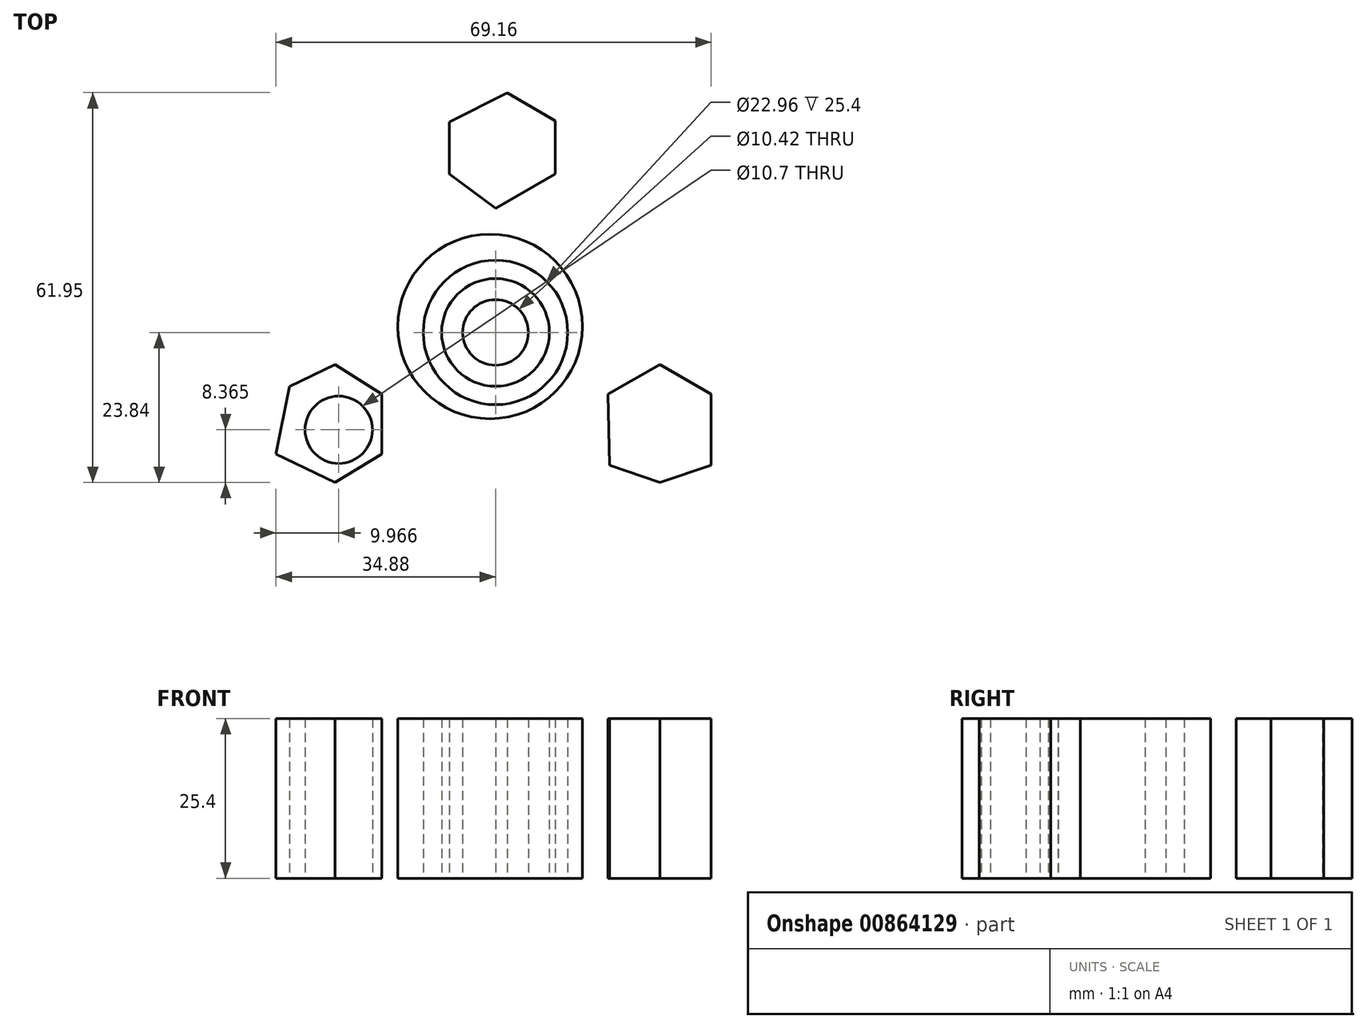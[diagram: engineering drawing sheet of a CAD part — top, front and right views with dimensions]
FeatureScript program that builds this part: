
annotation { "Feature Type Name" : "Feature", "Feature Type Description" : "" }
export const myFeature = defineFeature(function(context is Context, id is Id, definition is map)
    precondition{}
    {
        {
            var Q0;
            Q0=qCreatedBy(makeId("Top.planeOp"),FACE);
            var sketch = newSketch(context, id + "F0", { "sketchPlane" : qUnion([Q0])});
            skLineSegment(sketch, "E0", {"start": v(-11.04, 35.96) * mm, "end": v(-11.04, 44.95) * mm});
            skLineSegment(sketch, "E1", {"start": v(-11.04, 44.95) * mm, "end": v(-3.22, 42.4) * mm});
            skLineSegment(sketch, "E2", {"start": v(6.16, 42.4) * mm, "end": v(11.63, 44.95) * mm});
            skLineSegment(sketch, "E3", {"start": v(11.63, 44.95) * mm, "end": v(11.63, 37.52) * mm});
            skLineSegment(sketch, "E4", {"start": v(39.77, -8.2) * mm, "end": v(47.59, -14.27) * mm});
            skLineSegment(sketch, "E5", {"start": v(47.59, -14.27) * mm, "end": v(41.73, -18.37) * mm});
            skLineSegment(sketch, "E6", {"start": v(26.1, -31.66) * mm, "end": v(36.72, -37.23) * mm});
            skLineSegment(sketch, "E7", {"start": v(35.86, -27.75) * mm, "end": v(36.72, -37.23) * mm});
            skLineSegment(sketch, "E8", {"start": v(-37.62, -7.04) * mm, "end": v(-44.65, -12.7) * mm});
            skLineSegment(sketch, "E9", {"start": v(-44.65, -12.7) * mm, "end": v(-39.3, -15.5) * mm});
            skLineSegment(sketch, "E10", {"start": v(-34.88, -24.82) * mm, "end": v(-34.88, -32.05) * mm});
            skLineSegment(sketch, "E11", {"start": v(-34.88, -32.05) * mm, "end": v(-27.85, -29.12) * mm});
            skArc(sketch, "E12", {"start": v(-3.22, 42.4) * mm, "mid": v(1.47, 41.37) * mm, "end": v(6.16, 42.4) * mm});
            skArc(sketch, "E13", {"start": v(11.63, 16.8) * mm, "mid": v(15.34, 27.16) * mm, "end": v(11.63, 37.52) * mm});
            skArc(sketch, "E14", {"start": v(20.03, -2.35) * mm, "mid": v(19.22, 8.47) * mm, "end": v(11.63, 16.22) * mm});
            skArc(sketch, "E15", {"start": v(-11.04, 35.96) * mm, "mid": v(-13.25, 25.93) * mm, "end": v(-6.74, 17.98) * mm});
            skArc(sketch, "E16", {"start": v(-6.74, 17.98) * mm, "mid": v(-15.8, 11.02) * mm, "end": v(-18.86, 0) * mm});
            skArc(sketch, "E17", {"start": v(-18.86, 0) * mm, "mid": v(-29.8, 0.68) * mm, "end": v(-37.62, -7.04) * mm});
            skArc(sketch, "E18", {"start": v(-27.85, -29.12) * mm, "mid": v(-15.66, -27.36) * mm, "end": v(-10.84, -16.02) * mm});
            skArc(sketch, "E19", {"start": v(-10.84, -16.02) * mm, "mid": v(0.2, -21.41) * mm, "end": v(11.24, -16.02) * mm});
            skArc(sketch, "E20", {"start": v(11.24, -16.02) * mm, "mid": v(15.83, -26.53) * mm, "end": v(26.1, -31.66) * mm});
            skArc(sketch, "E21", {"start": v(39.38, -6.06) * mm, "mid": v(31.32, -1.24) * mm, "end": v(21.99, -2.35) * mm});
            skCircle(sketch, "E22", {"center": v(0, 0) * mm, "radius": 5.21 * mm});
            skCircle(sketch, "E23", {"center": v(0, 0) * mm, "radius": 8.56 * mm});
            skCircle(sketch, "E24", {"center": v(0, 0) * mm, "radius": 11.48 * mm});
            skCircle(sketch, "E25", {"center": v(-0.87, 0.95) * mm, "radius": 14.67 * mm});
            skLineSegment(sketch, "E26", {"start": v(-32.73, -8.6) * mm, "end": v(-25.5, -5.08) * mm});
            skLineSegment(sketch, "E27", {"start": v(-25.5, -5.08) * mm, "end": v(-18.07, -9.77) * mm});
            skLineSegment(sketch, "E28", {"start": v(-18.07, -9.77) * mm, "end": v(-18.07, -19.35) * mm});
            skLineSegment(sketch, "E29", {"start": v(-18.07, -19.35) * mm, "end": v(-25.5, -23.84) * mm});
            skLineSegment(sketch, "E30", {"start": v(-32.73, -8.6) * mm, "end": v(-34.88, -19.35) * mm});
            skLineSegment(sketch, "E31", {"start": v(-34.88, -19.35) * mm, "end": v(-25.5, -23.84) * mm});
            skLineSegment(sketch, "E32", {"start": v(17.88, -9.77) * mm, "end": v(26.1, -5.08) * mm});
            skLineSegment(sketch, "E33", {"start": v(26.1, -5.08) * mm, "end": v(34.28, -9.77) * mm});
            skLineSegment(sketch, "E34", {"start": v(34.28, -9.77) * mm, "end": v(34.28, -21.1) * mm});
            skLineSegment(sketch, "E35", {"start": v(34.28, -21.1) * mm, "end": v(26.1, -23.84) * mm});
            skLineSegment(sketch, "E36", {"start": v(26.1, -23.84) * mm, "end": v(18.14, -21.1) * mm});
            skLineSegment(sketch, "E37", {"start": v(18.14, -21.1) * mm, "end": v(17.88, -9.77) * mm});
            skCircle(sketch, "E38", {"center": v(25.31, -15.48) * mm, "radius": 6.67 * mm});
            skCircle(sketch, "E39", {"center": v(-24.91, -15.48) * mm, "radius": 5.35 * mm});
            skLineSegment(sketch, "E40", {"start": v(-7.33, 33.42) * mm, "end": v(-7.33, 25.2) * mm});
            skLineSegment(sketch, "E41", {"start": v(-7.33, 25.2) * mm, "end": v(0, 19.74) * mm});
            skLineSegment(sketch, "E42", {"start": v(0, 19.74) * mm, "end": v(9.48, 25.2) * mm});
            skLineSegment(sketch, "E43", {"start": v(9.48, 25.2) * mm, "end": v(9.48, 33.61) * mm});
            skLineSegment(sketch, "E44", {"start": v(9.48, 33.61) * mm, "end": v(1.86, 38.1) * mm});
            skLineSegment(sketch, "E45", {"start": v(1.86, 38.1) * mm, "end": v(-7.33, 33.42) * mm});
            skLineSegment(sketch, "E46", {"start": v(20.03, -2.35) * mm, "end": v(25.25, -1.24) * mm});
            skLineSegment(sketch, "E47", {"start": v(39.38, -6.06) * mm, "end": v(39.77, -8.2) * mm});
            skLineSegment(sketch, "E48", {"start": v(41.73, -18.37) * mm, "end": v(35.86, -27.75) * mm});
            skArc(sketch, "E49", {"start": v(-39.38, -17) * mm, "mid": v(-38.95, -21.96) * mm, "end": v(-34.88, -24.82) * mm});
            skSolve(sketch);
        }
        {
            var Q0;
            Q0=makeQuery(id+"F0.imprint","IMPRINT",FACE,{"disambiguationData":[TD([[makeQuery(id+"F0.imprint","IMPRINT",EDGE,{"derivedFrom":sQuery(id+"F0.wireOp",EDGE,"E24")}),-1.0]])]});
            var Q1;
            Q1=makeQuery(id+"F0.imprint","IMPRINT",FACE,{"disambiguationData":[TD([[makeQuery(id+"F0.imprint","IMPRINT",EDGE,{"derivedFrom":sQuery(id+"F0.wireOp",EDGE,"E22")}),-1.0]])]});
            var Q2;
            Q2=makeQuery(id+"F0.imprint","IMPRINT",FACE,{"disambiguationData":[TD([[makeQuery(id+"F0.imprint","IMPRINT",EDGE,{"derivedFrom":sQuery(id+"F0.wireOp",EDGE,"E32")}),-1.0]])]});
            var Q3;
            Q3=makeQuery(id+"F0.imprint","IMPRINT",FACE,{"disambiguationData":[TD([[makeQuery(id+"F0.imprint","IMPRINT",EDGE,{"derivedFrom":sQuery(id+"F0.wireOp",EDGE,"E38")}),1.0]])]});
            var Q4;
            Q4=makeQuery(id+"F0.imprint","IMPRINT",FACE,{"disambiguationData":[TD([[makeQuery(id+"F0.imprint","IMPRINT",EDGE,{"derivedFrom":sQuery(id+"F0.wireOp",EDGE,"E26")}),-1.0]])]});
            var Q5;
            Q5=makeQuery(id+"F0.imprint","IMPRINT",FACE,{"disambiguationData":[TD([[makeQuery(id+"F0.imprint","IMPRINT",EDGE,{"derivedFrom":sQuery(id+"F0.wireOp",EDGE,"E40")}),1.0]])]});
            extrude(context, id + "F1", {"entities" : qUnion([Q0, Q1, Q2, Q3, Q4, Q5]), "depth" : 25.4 * mm, "offsetDistance" : 25.4 * mm});
        }
    });
